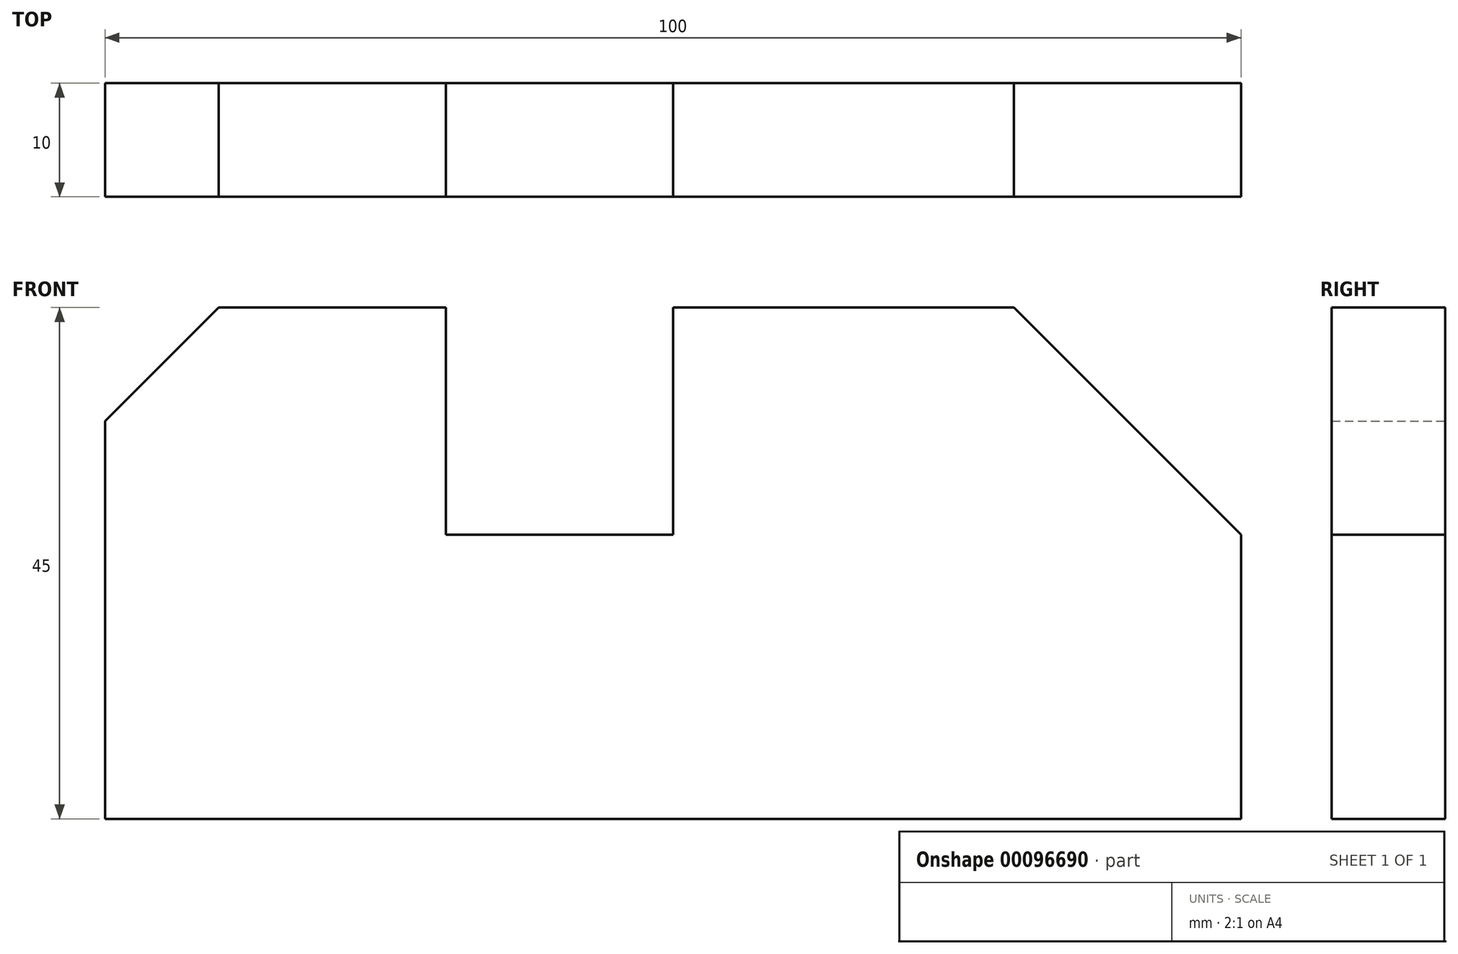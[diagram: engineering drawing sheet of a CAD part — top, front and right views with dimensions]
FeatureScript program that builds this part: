
annotation { "Feature Type Name" : "Feature", "Feature Type Description" : "" }
export const myFeature = defineFeature(function(context is Context, id is Id, definition is map)
    precondition{}
    {
        {
            var Q0;
            Q0=qCreatedBy(makeId("Front.planeOp"),FACE);
            var sketch = newSketch(context, id + "F0", { "sketchPlane" : qUnion([Q0])});
            skLineSegment(sketch, "E0", {"start": v(0, 0) * mm, "end": v(0, 35) * mm});
            skLineSegment(sketch, "E1", {"start": v(0, 35) * mm, "end": v(10, 45) * mm});
            skLineSegment(sketch, "E2", {"start": v(10, 45) * mm, "end": v(30, 45) * mm});
            skLineSegment(sketch, "E3", {"start": v(30, 45) * mm, "end": v(30, 25) * mm});
            skLineSegment(sketch, "E4", {"start": v(30, 25) * mm, "end": v(50, 25) * mm});
            skLineSegment(sketch, "E5", {"start": v(50, 25) * mm, "end": v(50, 45) * mm});
            skLineSegment(sketch, "E6", {"start": v(50, 45) * mm, "end": v(80, 45) * mm});
            skLineSegment(sketch, "E7", {"start": v(80, 45) * mm, "end": v(100, 25) * mm});
            skLineSegment(sketch, "E8", {"start": v(100, 25) * mm, "end": v(100, 0) * mm});
            skLineSegment(sketch, "E9", {"start": v(100, 0) * mm, "end": v(0, 0) * mm});
            skLineSegment(sketch, "E10", {"start": v(30, 45) * mm, "end": v(50, 45) * mm, "construction": true});
            skSolve(sketch);
        }
        {
            var Q0;
            Q0 = qSketchRegion(id + "F0", true);
            extrude(context, id + "F1", {"entities" : qUnion([Q0]), "depth" : 10 * mm});
        }
    });
